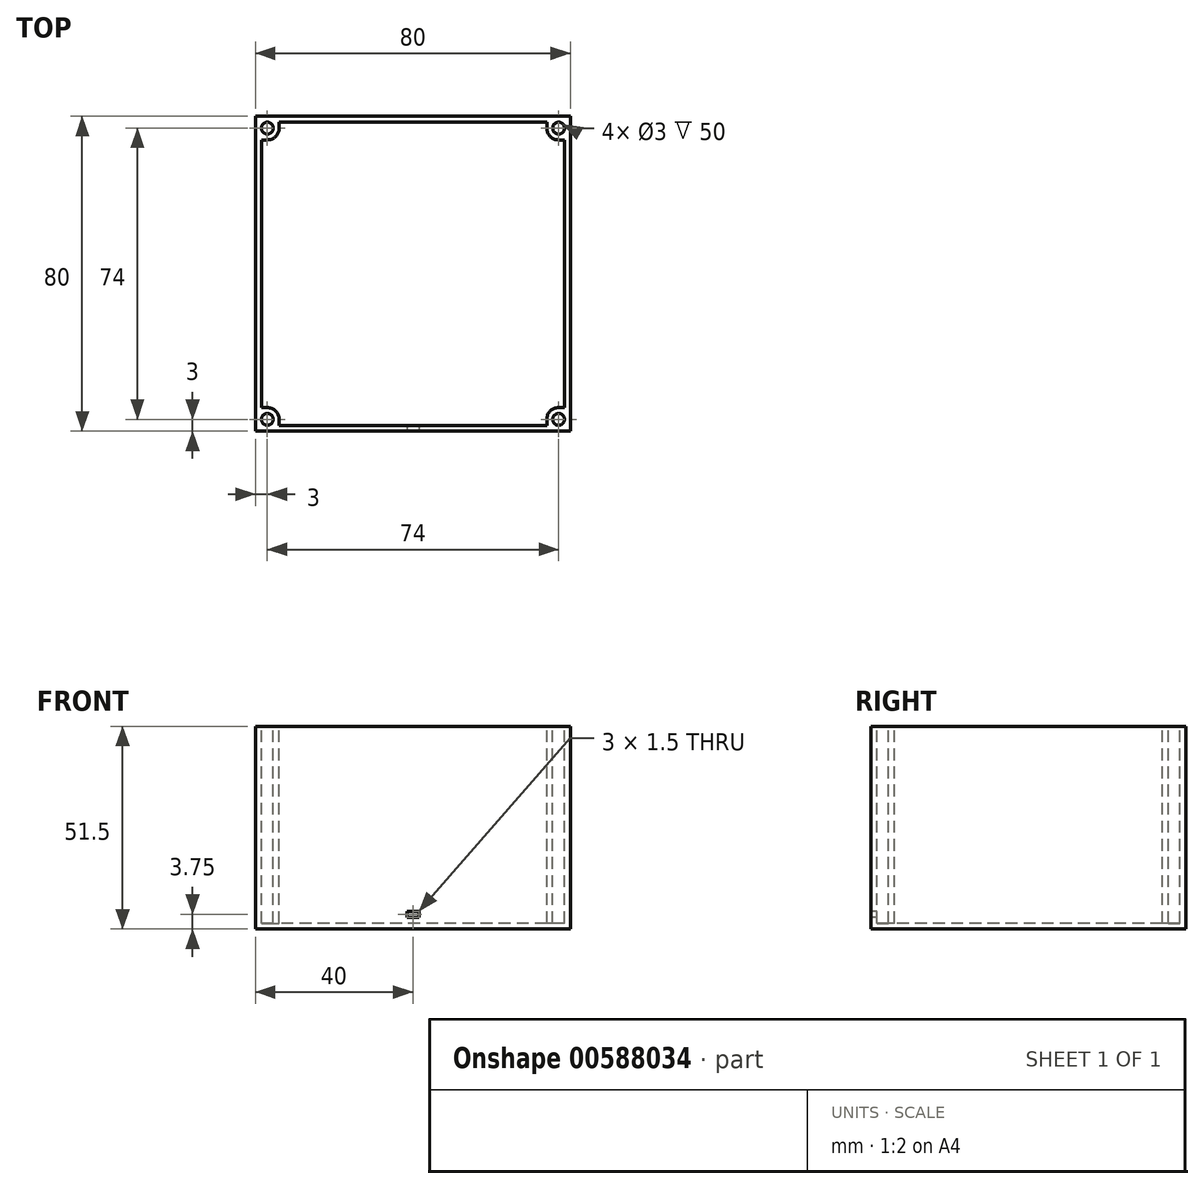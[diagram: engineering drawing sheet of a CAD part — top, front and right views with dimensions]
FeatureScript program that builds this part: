
annotation { "Feature Type Name" : "Feature", "Feature Type Description" : "" }
export const myFeature = defineFeature(function(context is Context, id is Id, definition is map)
    precondition{}
    {
        {
            var Q0;
            Q0=qCreatedBy(makeId("Top.planeOp"),FACE);
            var sketch = newSketch(context, id + "F0", { "sketchPlane" : qUnion([Q0])});
            skLineSegment(sketch, "E0.bottom", {"start": v(40, 40) * mm, "end": v(-40, 40) * mm});
            skLineSegment(sketch, "E0.top", {"start": v(40, -40) * mm, "end": v(-40, -40) * mm});
            skLineSegment(sketch, "E0.left", {"start": v(40, 40) * mm, "end": v(40, -40) * mm});
            skLineSegment(sketch, "E0.right", {"start": v(-40, 40) * mm, "end": v(-40, -40) * mm});
            skPoint(sketch, "E0.middle", {"position": v(0, 0) * mm});
            skSolve(sketch);
        }
        {
            var Q0;
            Q0=makeQuery(id+"F0.imprint","IMPRINT",FACE,{"disambiguationData":[TD([[makeQuery(id+"F0.imprint","IMPRINT",EDGE,{"derivedFrom":sQuery(id+"F0.wireOp",EDGE,"E0.bottom")}),1.0]])]});
            extrude(context, id + "F1", {"entities" : qUnion([Q0]), "depth" : 51.5 * mm, "offsetDistance" : 25 * mm});
        }
        {
            var Q0;
            Q0=makeQuery(id+"F1.opExtrude","CAP_FACE",FACE,{"disambiguationData":[OSD([sQuery(id+"F0.wireOp",EDGE,"E0.bottom"),sQuery(id+"F0.wireOp",EDGE,"E0.top"),sQuery(id+"F0.wireOp",EDGE,"E0.left"),sQuery(id+"F0.wireOp",EDGE,"E0.right")])],"isStart":false});
            shell(context, id + "F2", {"entities" : qUnion([Q0]), "thickness" : 1.5 * mm});
        }
        {
            var Q0;
            Q0=makeQuery(id+"F1.opExtrude","CAP_FACE",FACE,{"disambiguationData":[OSD([sQuery(id+"F0.wireOp",EDGE,"E0.bottom"),sQuery(id+"F0.wireOp",EDGE,"E0.top"),sQuery(id+"F0.wireOp",EDGE,"E0.left"),sQuery(id+"F0.wireOp",EDGE,"E0.right")])],"isStart":false});
            var sketch = newSketch(context, id + "F3", { "sketchPlane" : qUnion([Q0])});
            skCircle(sketch, "E1", {"center": v(-37, 37) * mm, "radius": 1.5 * mm});
            skArc(sketch, "E2.0", {"start": v(-37, 34) * mm, "mid": v(-34.88, 34.88) * mm, "end": v(-34, 37) * mm});
            skLineSegment(sketch, "E3.0", {"start": v(-38.5, 38.5) * mm, "end": v(-38.5, -38.5) * mm});
            skLineSegment(sketch, "E4.0", {"start": v(38.5, 38.5) * mm, "end": v(-38.5, 38.5) * mm});
            skLineSegment(sketch, "E5", {"start": v(-37, 34) * mm, "end": v(-38.5, 34) * mm});
            skLineSegment(sketch, "E6", {"start": v(-34, 37) * mm, "end": v(-34, 38.5) * mm});
            skLineSegment(sketch, "E7.0", {"start": v(38.5, 38.5) * mm, "end": v(38.5, -38.5) * mm});
            skLineSegment(sketch, "E8.0", {"start": v(38.5, -38.5) * mm, "end": v(-38.5, -38.5) * mm});
            skCircle(sketch, "E9", {"center": v(-37, -37) * mm, "radius": 1.5 * mm});
            skCircle(sketch, "E10", {"center": v(37, -37) * mm, "radius": 1.5 * mm});
            skCircle(sketch, "E11", {"center": v(37, 37) * mm, "radius": 1.5 * mm});
            skArc(sketch, "E12.0", {"start": v(34, 37) * mm, "mid": v(34.88, 34.88) * mm, "end": v(37, 34) * mm});
            skArc(sketch, "E13", {"start": v(-34, -37) * mm, "mid": v(-34.88, -34.88) * mm, "end": v(-37, -34) * mm});
            skArc(sketch, "E14", {"start": v(37, -34) * mm, "mid": v(34.88, -34.88) * mm, "end": v(34, -37) * mm});
            skLineSegment(sketch, "E15", {"start": v(37, 34) * mm, "end": v(38.5, 34) * mm});
            skLineSegment(sketch, "E16", {"start": v(34, 37) * mm, "end": v(34, 38.5) * mm});
            skLineSegment(sketch, "E17", {"start": v(37, -34) * mm, "end": v(38.5, -34) * mm});
            skLineSegment(sketch, "E18", {"start": v(34, -37) * mm, "end": v(34, -38.5) * mm});
            skLineSegment(sketch, "E19", {"start": v(-34, -37) * mm, "end": v(-34, -38.5) * mm});
            skLineSegment(sketch, "E20", {"start": v(-37, -34) * mm, "end": v(-38.5, -34) * mm});
            skSolve(sketch);
        }
        {
            var Q0;
            Q0=makeQuery(id+"F3.imprint","IMPRINT",FACE,{"disambiguationData":[TD([[makeQuery(id+"F3.imprint","IMPRINT",EDGE,{"derivedFrom":sQuery(id+"F3.wireOp",EDGE,"E2.0")}),1.0]])]});
            var Q1;
            {var subQ0=sQuery(id+"F3.wireOp",EDGE,"E3.0");var subQ1=sQuery(id+"F3.wireOp",EDGE,"E1");var subQ2=makeQuery(id+"F3.imprint","INTERSECT",VERTEX,{"derivedFrom":[subQ1,subQ0]});Q1=makeQuery(id+"F3.imprint","IMPRINT",FACE,{"disambiguationData":[TD([[makeQuery(id+"F3.imprint","IMPRINT",EDGE,{"disambiguationData":[TD([[subQ2,1.0]])],"derivedFrom":subQ1}),-1.0]])]});}
            var Q2;
            Q2=makeQuery(id+"F3.imprint","IMPRINT",FACE,{"disambiguationData":[TD([[makeQuery(id+"F3.imprint","IMPRINT",EDGE,{"derivedFrom":sQuery(id+"F3.wireOp",EDGE,"E13")}),1.0]])]});
            var Q3;
            {var subQ0=sQuery(id+"F3.wireOp",EDGE,"E8.0");var subQ1=sQuery(id+"F3.wireOp",EDGE,"E3.0");var subQ2=makeQuery(id+"F3.imprint","INTERSECT",VERTEX,{"derivedFrom":[subQ1,subQ0]});Q3=makeQuery(id+"F3.imprint","IMPRINT",FACE,{"disambiguationData":[TD([[makeQuery(id+"F3.imprint","IMPRINT",EDGE,{"disambiguationData":[TD([[subQ2,1.0]])],"derivedFrom":subQ1}),1.0]])]});}
            var Q4;
            Q4=makeQuery(id+"F3.imprint","IMPRINT",FACE,{"disambiguationData":[TD([[makeQuery(id+"F3.imprint","IMPRINT",EDGE,{"derivedFrom":sQuery(id+"F3.wireOp",EDGE,"E14")}),1.0]])]});
            var Q5;
            {var subQ0=sQuery(id+"F3.wireOp",EDGE,"E8.0");var subQ1=sQuery(id+"F3.wireOp",EDGE,"E7.0");var subQ2=makeQuery(id+"F3.imprint","INTERSECT",VERTEX,{"derivedFrom":[subQ1,subQ0]});Q5=makeQuery(id+"F3.imprint","IMPRINT",FACE,{"disambiguationData":[TD([[makeQuery(id+"F3.imprint","IMPRINT",EDGE,{"disambiguationData":[TD([[subQ2,1.0]])],"derivedFrom":subQ1}),-1.0]])]});}
            var Q6;
            Q6=makeQuery(id+"F3.imprint","IMPRINT",FACE,{"disambiguationData":[TD([[makeQuery(id+"F3.imprint","IMPRINT",EDGE,{"derivedFrom":sQuery(id+"F3.wireOp",EDGE,"E12.0")}),1.0]])]});
            var Q7;
            {var subQ0=sQuery(id+"F3.wireOp",EDGE,"E7.0");var subQ1=sQuery(id+"F3.wireOp",EDGE,"E4.0");var subQ2=makeQuery(id+"F3.imprint","INTERSECT",VERTEX,{"derivedFrom":[subQ1,subQ0]});Q7=makeQuery(id+"F3.imprint","IMPRINT",FACE,{"disambiguationData":[TD([[makeQuery(id+"F3.imprint","IMPRINT",EDGE,{"disambiguationData":[TD([[subQ2,-1.0]])],"derivedFrom":subQ1}),1.0]])]});}
            extrude(context, id + "F4", {"entities" : qUnion([Q0, Q1, Q2, Q3, Q4, Q5, Q6, Q7]), "operationType" : NewBodyOperationType.ADD, "endBound" : BoundingType.UP_TO_NEXT, "oppositeDirection" : true, "depth" : 25 * mm, "offsetDistance" : 25 * mm});
        }
        {
            var Q0;
            Q0=makeQuery(id+"F1.opExtrude","SWEPT_FACE",FACE,{"disambiguationData":[OSD([sQuery(id+"F0.wireOp",EDGE,"E0.top")])]});
            var sketch = newSketch(context, id + "F5", { "sketchPlane" : qUnion([Q0])});
            skLineSegment(sketch, "E21", {"start": v(0, 0) * mm, "end": v(0, 51.5) * mm, "construction": true});
            skLineSegment(sketch, "E22.bottom", {"start": v(1.5, 4.5) * mm, "end": v(-1.5, 4.5) * mm});
            skLineSegment(sketch, "E22.top", {"start": v(1.5, 3) * mm, "end": v(-1.5, 3) * mm});
            skLineSegment(sketch, "E22.left", {"start": v(1.5, 4.5) * mm, "end": v(1.5, 3) * mm});
            skLineSegment(sketch, "E22.right", {"start": v(-1.5, 4.5) * mm, "end": v(-1.5, 3) * mm});
            skPoint(sketch, "E22.middle", {"position": v(0, 3.75) * mm});
            skSolve(sketch);
        }
        {
            var Q0;
            Q0=makeQuery(id+"F5.imprint","IMPRINT",FACE,{"disambiguationData":[TD([[makeQuery(id+"F5.imprint","IMPRINT",EDGE,{"derivedFrom":sQuery(id+"F5.wireOp",EDGE,"E22.bottom")}),1.0]])]});
            extrude(context, id + "F6", {"entities" : qUnion([Q0]), "operationType" : NewBodyOperationType.REMOVE, "endBound" : BoundingType.UP_TO_NEXT, "oppositeDirection" : true, "depth" : 25 * mm, "offsetDistance" : 25 * mm});
        }
    });
